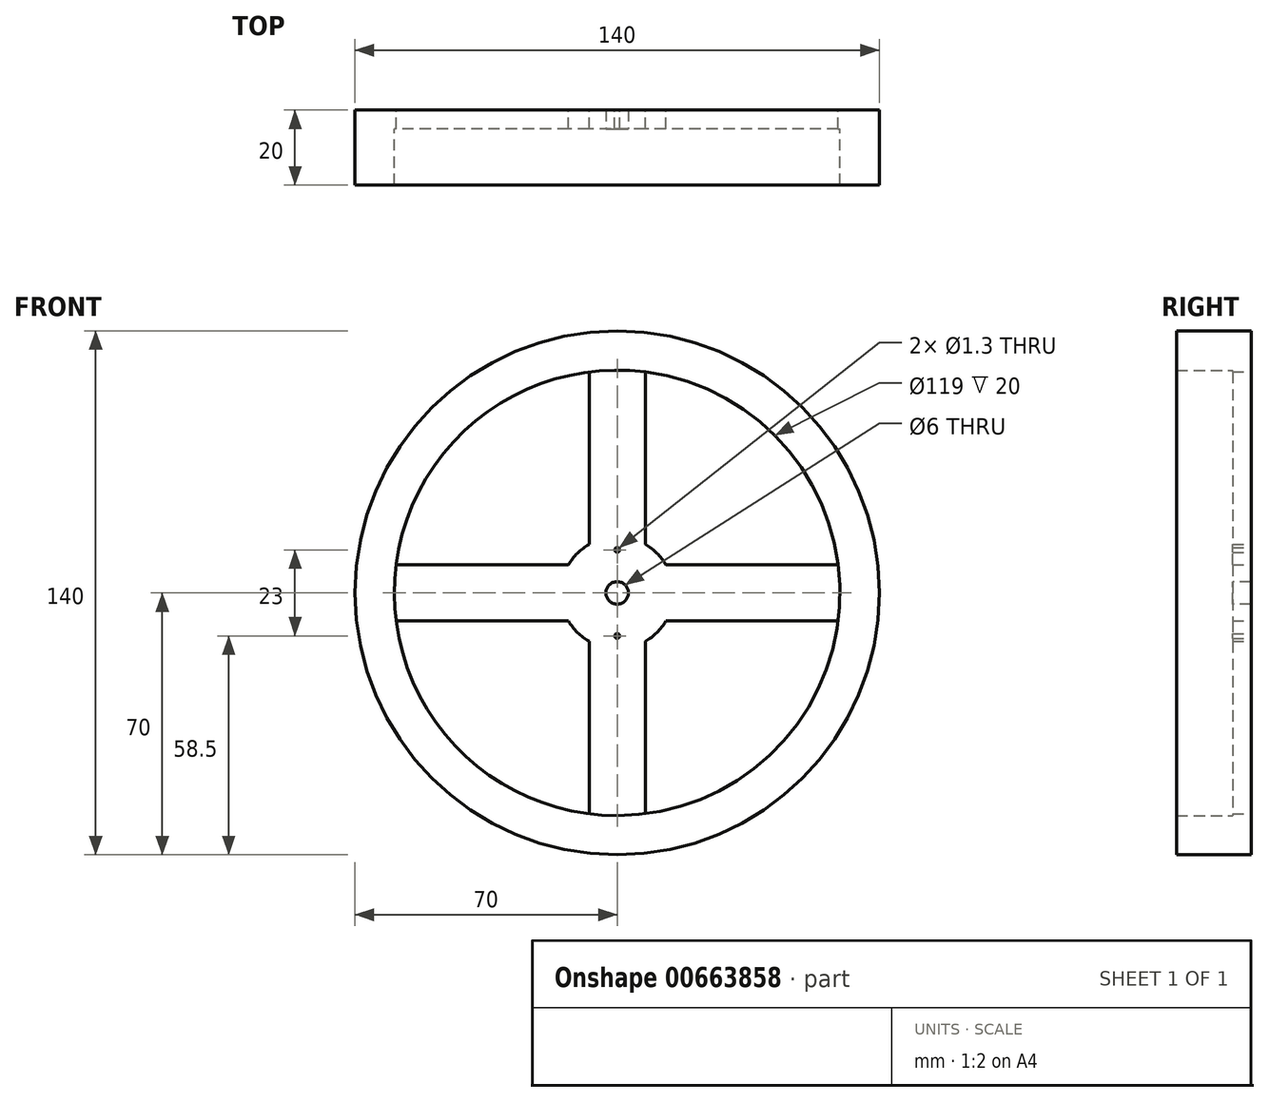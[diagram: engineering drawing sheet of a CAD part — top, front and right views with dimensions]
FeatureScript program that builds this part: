
annotation { "Feature Type Name" : "Feature", "Feature Type Description" : "" }
export const myFeature = defineFeature(function(context is Context, id is Id, definition is map)
    precondition{}
    {
        {
            assignVariable(context, id + "F0", {"name" : "insideWidth", "anyValue" : 5});
        }
        {
            assignVariable(context, id + "F1", {"name" : "outsideWidth", "anyValue" : 20});
        }
        {
            var Q0;
            Q0=qCreatedBy(makeId("Front.planeOp"),FACE);
            var sketch = newSketch(context, id + "F2", { "sketchPlane" : qUnion([Q0])});
            skCircle(sketch, "E0", {"center": v(0, 0) * mm, "radius": 70 * mm});
            skCircle(sketch, "E1", {"center": v(0, 0) * mm, "radius": 59.5 * mm});
            skSolve(sketch);
        }
        {
            var Q0;
            Q0 = qSketchRegion(id + "F2", true);
            var Q1;
            Q1=makeQuery(id+"F2.imprint","IMPRINT",FACE,{"disambiguationData":[TD([[makeQuery(id+"F2.imprint","IMPRINT",EDGE,{"derivedFrom":sQuery(id+"F2.wireOp",EDGE,"E0")}),1.0]])]});
            extrude(context, id + "F3", {"entities" : qUnion([Q0, Q1]), "depth" : (getVariable(context, 'outsideWidth')) * mm, "offsetDistance" : 25 * mm});
        }
        {
            var Q0;
            Q0=qCreatedBy(makeId("Front.planeOp"),FACE);
            var sketch = newSketch(context, id + "F4", { "sketchPlane" : qUnion([Q0])});
            skCircle(sketch, "E2", {"center": v(0, 0) * mm, "radius": 15 * mm});
            skSolve(sketch);
        }
        {
            var Q0;
            Q0 = qSketchRegion(id + "F4", true);
            extrude(context, id + "F5", {"entities" : qUnion([Q0]), "depth" : (getVariable(context, 'insideWidth')) * mm, "offsetDistance" : 25 * mm});
        }
        {
            var Q0;
            Q0=qCreatedBy(makeId("Front.planeOp"),FACE);
            var sketch = newSketch(context, id + "F6", { "sketchPlane" : qUnion([Q0])});
            skLineSegment(sketch, "E3.bottom", {"start": v(65, 7.5) * mm, "end": v(-65, 7.5) * mm});
            skLineSegment(sketch, "E3.top", {"start": v(65, -7.5) * mm, "end": v(-65, -7.5) * mm});
            skLineSegment(sketch, "E3.left", {"start": v(65, 7.5) * mm, "end": v(65, -7.5) * mm});
            skLineSegment(sketch, "E3.right", {"start": v(-65, 7.5) * mm, "end": v(-65, -7.5) * mm});
            skPoint(sketch, "E3.middle", {"position": v(0, 0) * mm});
            skSolve(sketch);
        }
        {
            var Q0;
            Q0=makeQuery(id+"F6.imprint","IMPRINT",FACE,{"disambiguationData":[TD([[makeQuery(id+"F6.imprint","IMPRINT",EDGE,{"derivedFrom":sQuery(id+"F6.wireOp",EDGE,"E3.bottom")}),1.0]])]});
            extrude(context, id + "F7", {"entities" : qUnion([Q0]), "depth" : (getVariable(context, 'insideWidth')) * mm, "offsetDistance" : 25 * mm});
        }
        {
            var Q0;
            Q0=qCreatedBy(makeId("Front.planeOp"),FACE);
            var sketch = newSketch(context, id + "F8", { "sketchPlane" : qUnion([Q0])});
            skLineSegment(sketch, "E4.bottom", {"start": v(7.5, 65) * mm, "end": v(-7.5, 65) * mm});
            skLineSegment(sketch, "E4.top", {"start": v(7.5, -65) * mm, "end": v(-7.5, -65) * mm});
            skLineSegment(sketch, "E4.left", {"start": v(7.5, 65) * mm, "end": v(7.5, -65) * mm});
            skLineSegment(sketch, "E4.right", {"start": v(-7.5, 65) * mm, "end": v(-7.5, -65) * mm});
            skPoint(sketch, "E4.middle", {"position": v(0, 0) * mm});
            skSolve(sketch);
        }
        {
            var Q0;
            Q0 = qSketchRegion(id + "F8", true);
            extrude(context, id + "F9", {"entities" : qUnion([Q0]), "depth" : (getVariable(context, 'insideWidth')) * mm, "offsetDistance" : 25 * mm});
        }
        {
            var Q0;
            Q0=makeQuery(id+"F3.opExtrude","SWEPT_BODY",BODY,{"disambiguationData":[OSD([sQuery(id+"F2.wireOp",EDGE,"E0"),sQuery(id+"F2.wireOp",EDGE,"E1")])]});
            var Q1;
            Q1=makeQuery(id+"F5.opExtrude","SWEPT_BODY",BODY,{"disambiguationData":[OSD([sQuery(id+"F4.wireOp",EDGE,"E2")])]});
            var Q2;
            Q2=makeQuery(id+"F7.opExtrude","SWEPT_BODY",BODY,{"disambiguationData":[OSD([sQuery(id+"F6.wireOp",EDGE,"E3.bottom"),sQuery(id+"F6.wireOp",EDGE,"E3.top"),sQuery(id+"F6.wireOp",EDGE,"E3.left"),sQuery(id+"F6.wireOp",EDGE,"E3.right")])]});
            var Q3;
            Q3=makeQuery(id+"F9.opExtrude","SWEPT_BODY",BODY,{"disambiguationData":[OSD([sQuery(id+"F8.wireOp",EDGE,"E4.bottom"),sQuery(id+"F8.wireOp",EDGE,"E4.top"),sQuery(id+"F8.wireOp",EDGE,"E4.left"),sQuery(id+"F8.wireOp",EDGE,"E4.right")])]});
            booleanBodies(context, id + "F10", {"operationType" : BooleanOperationType.UNION, "tools" : qUnion([Q0, Q1, Q2, Q3])});
        }
        {
            var Q0;
            Q0=makeQuery(id+"F10.opBoolean","MERGE",FACE,{"derivedFrom":[makeQuery(id+"F5.opExtrude","CAP_FACE",FACE,{"disambiguationData":[OSD([sQuery(id+"F4.wireOp",EDGE,"E2")])],"isStart":false}),makeQuery(id+"F7.opExtrude","CAP_FACE",FACE,{"disambiguationData":[OSD([sQuery(id+"F6.wireOp",EDGE,"E3.bottom"),sQuery(id+"F6.wireOp",EDGE,"E3.top"),sQuery(id+"F6.wireOp",EDGE,"E3.left"),sQuery(id+"F6.wireOp",EDGE,"E3.right")])],"isStart":false}),makeQuery(id+"F9.opExtrude","CAP_FACE",FACE,{"disambiguationData":[OSD([sQuery(id+"F8.wireOp",EDGE,"E4.bottom"),sQuery(id+"F8.wireOp",EDGE,"E4.top"),sQuery(id+"F8.wireOp",EDGE,"E4.left"),sQuery(id+"F8.wireOp",EDGE,"E4.right")])],"isStart":false})]});
            var sketch = newSketch(context, id + "F11", { "sketchPlane" : qUnion([Q0])});
            skCircle(sketch, "E5", {"center": v(0, 0) * mm, "radius": 3 * mm});
            skSolve(sketch);
        }
        {
            var Q0;
            Q0 = qSketchRegion(id + "F11", true);
            extrude(context, id + "F12", {"entities" : qUnion([Q0]), "operationType" : NewBodyOperationType.REMOVE, "endBound" : BoundingType.THROUGH_ALL, "oppositeDirection" : true, "depth" : 84.1 * mm, "offsetDistance" : 25 * mm});
        }
        {
            var Q0;
            Q0=qCreatedBy(makeId("Front.planeOp"),FACE);
            var sketch = newSketch(context, id + "F13", { "sketchPlane" : qUnion([Q0])});
            skLineSegment(sketch, "E6", {"start": v(0, 11.5) * mm, "end": v(0, -11.5) * mm});
            skCircle(sketch, "E7", {"center": v(0, 11.5) * mm, "radius": 0.65 * mm});
            skCircle(sketch, "E8", {"center": v(0, -11.5) * mm, "radius": 0.65 * mm});
            skSolve(sketch);
        }
        {
            var Q0;
            Q0 = qSketchRegion(id + "F13", true);
            extrude(context, id + "F14", {"entities" : qUnion([Q0]), "operationType" : NewBodyOperationType.REMOVE, "oppositeDirection" : true, "depth" : -25 * mm, "offsetDistance" : 25 * mm});
        }
    });
